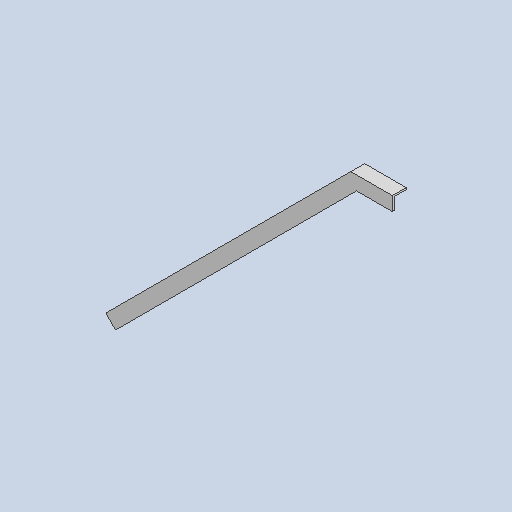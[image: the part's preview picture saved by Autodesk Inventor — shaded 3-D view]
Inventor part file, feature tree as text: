
AUTODESK INVENTOR PART (.ipt)
format: ipt  version: 2023 (Build 270158030, 158C)  size: 95,232 bytes
history: native  units: in
note: dims shown in document units (in); Inventor stores cm internally (conversion verified against a paired STEP export)
features: extrude x2, sketch x1
ambient origin geometry x8: Origin, YZ Plane, XZ Plane, XY Plane, X Axis, Y Axis, Z Axis, Center Point
bodies: Solid1 (feature_tree)
feature tree (3):
  sketch  "Sketch1"  dims[d0=12.5in d1=45.0deg d2=1.5in d3=0.5in d4=0.5in d5=90.0deg d6=0.0625in d7=0.0in d8=0.0625in d9=0.0625in d10=0.4375in d11=0.0in]
  extrude  "Extrusion1"  TaperAngle=45.0deg  [1 undecoded]
  extrude  "Extrusion2"  Depth=0.4375in
note: 1 required parameter value undecoded (feature->parameter linkage not recoverable at this tier; creation-order binding heuristic only, values carry confidence <= 0.55)
